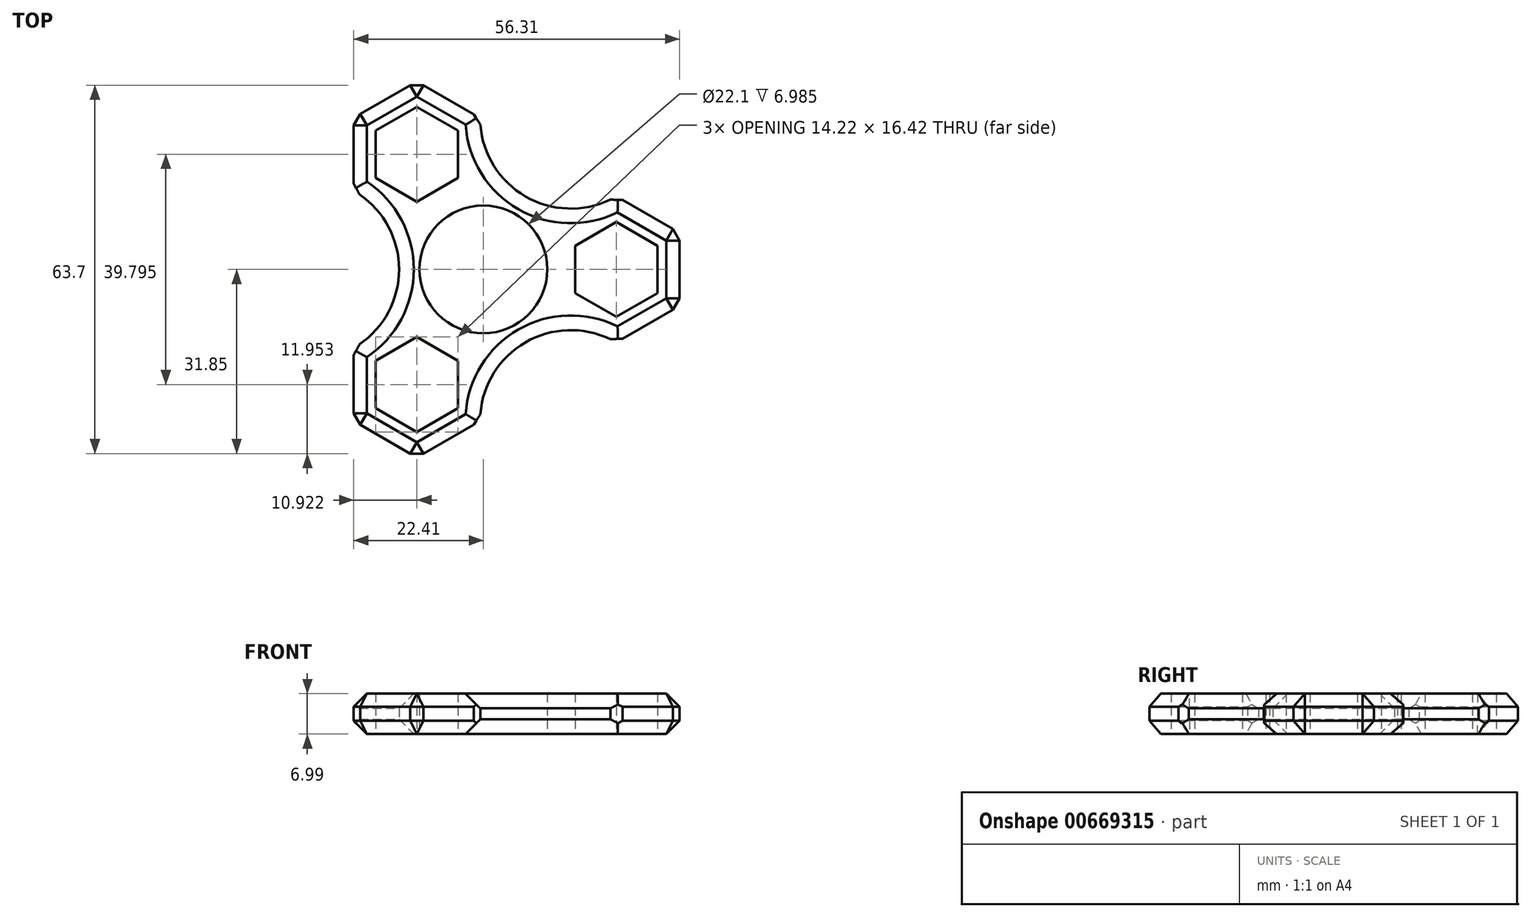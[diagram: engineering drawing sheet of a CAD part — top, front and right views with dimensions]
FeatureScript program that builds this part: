
annotation { "Feature Type Name" : "Feature", "Feature Type Description" : "" }
export const myFeature = defineFeature(function(context is Context, id is Id, definition is map)
    precondition{}
    {
        {
            var Q0;
            Q0=qCreatedBy(makeId("Top.planeOp"),FACE);
            var sketch = newSketch(context, id + "F0", { "sketchPlane" : qUnion([Q0])});
            skCircle(sketch, "E0", {"center": v(0, 0) * mm, "radius": 11.05 * mm});
            skLineSegment(sketch, "E1.0", {"start": v(15.86, -4.1) * mm, "end": v(15.86, 4.1) * mm});
            skLineSegment(sketch, "E1.1", {"start": v(15.86, 4.1) * mm, "end": v(22.98, 8.21) * mm});
            skLineSegment(sketch, "E1.2", {"start": v(22.98, 8.21) * mm, "end": v(30.09, 4.1) * mm});
            skLineSegment(sketch, "E1.3", {"start": v(30.09, 4.1) * mm, "end": v(30.09, -4.1) * mm});
            skLineSegment(sketch, "E1.4", {"start": v(30.09, -4.1) * mm, "end": v(22.98, -8.21) * mm});
            skLineSegment(sketch, "E1.5", {"start": v(22.98, -8.21) * mm, "end": v(15.86, -4.1) * mm});
            skPoint(sketch, "E1.0.midPoint", {"position": v(15.86, 0) * mm});
            skPoint(sketch, "E2.1.0", {"position": v(-7.93, 13.74) * mm});
            skLineSegment(sketch, "E2.1.1", {"start": v(-4.38, 24) * mm, "end": v(-4.38, 15.8) * mm});
            skLineSegment(sketch, "E2.1.2", {"start": v(-11.49, 28.1) * mm, "end": v(-4.38, 24) * mm});
            skLineSegment(sketch, "E2.1.3", {"start": v(-18.6, 24) * mm, "end": v(-11.49, 28.1) * mm});
            skLineSegment(sketch, "E2.1.4", {"start": v(-18.6, 15.8) * mm, "end": v(-18.6, 24) * mm});
            skLineSegment(sketch, "E2.1.5", {"start": v(-11.49, 11.69) * mm, "end": v(-18.6, 15.8) * mm});
            skLineSegment(sketch, "E2.1.6", {"start": v(-4.38, 15.8) * mm, "end": v(-11.49, 11.69) * mm});
            skPoint(sketch, "E2.2.0", {"position": v(-7.93, -13.74) * mm});
            skLineSegment(sketch, "E2.2.1", {"start": v(-18.6, -15.8) * mm, "end": v(-11.49, -11.69) * mm});
            skLineSegment(sketch, "E2.2.2", {"start": v(-18.6, -24) * mm, "end": v(-18.6, -15.8) * mm});
            skLineSegment(sketch, "E2.2.3", {"start": v(-11.49, -28.1) * mm, "end": v(-18.6, -24) * mm});
            skLineSegment(sketch, "E2.2.4", {"start": v(-4.38, -24) * mm, "end": v(-11.49, -28.1) * mm});
            skLineSegment(sketch, "E2.2.5", {"start": v(-4.38, -15.8) * mm, "end": v(-4.38, -24) * mm});
            skLineSegment(sketch, "E2.2.6", {"start": v(-11.49, -11.69) * mm, "end": v(-4.38, -15.8) * mm});
            skLineSegment(sketch, "E3.0", {"start": v(-0.57, 26.2) * mm, "end": v(-0.57, 26.2) * mm});
            skLineSegment(sketch, "E3.2", {"start": v(-22.4, 13.6) * mm, "end": v(-22.4, 26.2) * mm});
            skLineSegment(sketch, "E3.4", {"start": v(-22.4, 26.2) * mm, "end": v(-11.49, 32.5) * mm});
            skLineSegment(sketch, "E3.5", {"start": v(-11.49, 32.5) * mm, "end": v(-0.57, 26.2) * mm});
            skLineSegment(sketch, "E4.2", {"start": v(22.98, 12.61) * mm, "end": v(33.9, 6.3) * mm});
            skLineSegment(sketch, "E4.4", {"start": v(33.9, 6.3) * mm, "end": v(33.9, -6.3) * mm});
            skLineSegment(sketch, "E4.5", {"start": v(33.9, -6.3) * mm, "end": v(22.98, -12.6) * mm});
            skLineSegment(sketch, "E5.0", {"start": v(-0.57, -26.2) * mm, "end": v(-11.49, -32.5) * mm});
            skLineSegment(sketch, "E5.1", {"start": v(-22.4, -26.2) * mm, "end": v(-22.4, -13.6) * mm});
            skLineSegment(sketch, "E5.3", {"start": v(-11.49, -32.5) * mm, "end": v(-22.4, -26.2) * mm});
            skArc(sketch, "E6", {"start": v(-22.4, -13.6) * mm, "mid": v(-14.56, 0) * mm, "end": v(-22.4, 13.6) * mm});
            skArc(sketch, "E7", {"start": v(22.98, -12.6) * mm, "mid": v(7.28, -12.6) * mm, "end": v(-0.57, -26.2) * mm});
            skArc(sketch, "E8", {"start": v(-0.57, 26.2) * mm, "mid": v(7.28, 12.61) * mm, "end": v(22.98, 12.61) * mm});
            skSolve(sketch);
        }
        {
            var Q0;
            Q0=makeQuery(id+"F0.imprint","IMPRINT",FACE,{"disambiguationData":[TD([[makeQuery(id+"F0.imprint","IMPRINT",EDGE,{"derivedFrom":sQuery(id+"F0.wireOp",EDGE,"E0")}),-1.0]])]});
            extrude(context, id + "F1", {"entities" : qUnion([Q0]), "depth" : 7 * mm, "offsetDistance" : 25.4 * mm});
        }
        {
            var Q0;
            Q0=makeQuery(id+"F1.opExtrude","CAP_EDGE",EDGE,{"disambiguationData":[OSD([sQuery(id+"F0.wireOp",EDGE,"E3.5")])],"isStart":true});
            var Q1;
            Q1=makeQuery(id+"F1.opExtrude","CAP_EDGE",EDGE,{"disambiguationData":[OSD([sQuery(id+"F0.wireOp",EDGE,"E3.4")])],"isStart":true});
            var Q2;
            Q2=makeQuery(id+"F1.opExtrude","CAP_EDGE",EDGE,{"disambiguationData":[OSD([sQuery(id+"F0.wireOp",EDGE,"E3.2")])],"isStart":true});
            var Q3;
            Q3=makeQuery(id+"F1.opExtrude","CAP_EDGE",EDGE,{"disambiguationData":[OSD([sQuery(id+"F0.wireOp",EDGE,"E5.3")])],"isStart":true});
            var Q4;
            Q4=makeQuery(id+"F1.opExtrude","CAP_EDGE",EDGE,{"disambiguationData":[OSD([sQuery(id+"F0.wireOp",EDGE,"E5.1")])],"isStart":true});
            var Q5;
            Q5=makeQuery(id+"F1.opExtrude","CAP_EDGE",EDGE,{"disambiguationData":[OSD([sQuery(id+"F0.wireOp",EDGE,"E5.0")])],"isStart":true});
            var Q6;
            Q6=makeQuery(id+"F1.opExtrude","CAP_EDGE",EDGE,{"disambiguationData":[OSD([sQuery(id+"F0.wireOp",EDGE,"E4.5")])],"isStart":true});
            var Q7;
            Q7=makeQuery(id+"F1.opExtrude","CAP_EDGE",EDGE,{"disambiguationData":[OSD([sQuery(id+"F0.wireOp",EDGE,"E4.4")])],"isStart":true});
            var Q8;
            Q8=makeQuery(id+"F1.opExtrude","CAP_EDGE",EDGE,{"disambiguationData":[OSD([sQuery(id+"F0.wireOp",EDGE,"E4.2")])],"isStart":true});
            var Q9;
            Q9=makeQuery(id+"F1.opExtrude","CAP_EDGE",EDGE,{"disambiguationData":[OSD([sQuery(id+"F0.wireOp",EDGE,"E3.5")])],"isStart":false});
            var Q10;
            Q10=makeQuery(id+"F1.opExtrude","CAP_EDGE",EDGE,{"disambiguationData":[OSD([sQuery(id+"F0.wireOp",EDGE,"E3.4")])],"isStart":false});
            var Q11;
            Q11=makeQuery(id+"F1.opExtrude","CAP_EDGE",EDGE,{"disambiguationData":[OSD([sQuery(id+"F0.wireOp",EDGE,"E3.2")])],"isStart":false});
            var Q12;
            Q12=makeQuery(id+"F1.opExtrude","CAP_EDGE",EDGE,{"disambiguationData":[OSD([sQuery(id+"F0.wireOp",EDGE,"E4.2")])],"isStart":false});
            var Q13;
            Q13=makeQuery(id+"F1.opExtrude","CAP_EDGE",EDGE,{"disambiguationData":[OSD([sQuery(id+"F0.wireOp",EDGE,"E4.4")])],"isStart":false});
            var Q14;
            Q14=makeQuery(id+"F1.opExtrude","CAP_EDGE",EDGE,{"disambiguationData":[OSD([sQuery(id+"F0.wireOp",EDGE,"E4.5")])],"isStart":false});
            var Q15;
            Q15=makeQuery(id+"F1.opExtrude","SWEPT_EDGE",EDGE,{"disambiguationData":[OSD([sQuery(id+"F0.wireOp",EDGE,"E4.4"),sQuery(id+"F0.wireOp",EDGE,"E4.5")])]});
            var Q16;
            Q16=makeQuery(id+"F1.opExtrude","CAP_EDGE",EDGE,{"disambiguationData":[OSD([sQuery(id+"F0.wireOp",EDGE,"E5.0")])],"isStart":false});
            var Q17;
            Q17=makeQuery(id+"F1.opExtrude","CAP_EDGE",EDGE,{"disambiguationData":[OSD([sQuery(id+"F0.wireOp",EDGE,"E5.3")])],"isStart":false});
            var Q18;
            Q18=makeQuery(id+"F1.opExtrude","CAP_EDGE",EDGE,{"disambiguationData":[OSD([sQuery(id+"F0.wireOp",EDGE,"E5.1")])],"isStart":false});
            var Q19;
            Q19=makeQuery(id+"F1.opExtrude","SWEPT_EDGE",EDGE,{"disambiguationData":[OSD([sQuery(id+"F0.wireOp",EDGE,"E4.2"),sQuery(id+"F0.wireOp",EDGE,"E4.4")])]});
            var Q20;
            Q20=makeQuery(id+"F1.opExtrude","SWEPT_EDGE",EDGE,{"disambiguationData":[OSD([sQuery(id+"F0.wireOp",EDGE,"E4.2"),sQuery(id+"F0.wireOp",EDGE,"E8")])]});
            var Q21;
            Q21=makeQuery(id+"F1.opExtrude","SWEPT_EDGE",EDGE,{"disambiguationData":[OSD([sQuery(id+"F0.wireOp",EDGE,"E4.5"),sQuery(id+"F0.wireOp",EDGE,"E7")])]});
            var Q22;
            Q22=makeQuery(id+"F1.opExtrude","SWEPT_EDGE",EDGE,{"disambiguationData":[OSD([sQuery(id+"F0.wireOp",EDGE,"E3.4"),sQuery(id+"F0.wireOp",EDGE,"E3.5")])]});
            var Q23;
            Q23=makeQuery(id+"F1.opExtrude","SWEPT_EDGE",EDGE,{"disambiguationData":[OSD([sQuery(id+"F0.wireOp",EDGE,"E3.2"),sQuery(id+"F0.wireOp",EDGE,"E3.4")])]});
            var Q24;
            Q24=makeQuery(id+"F1.opExtrude","SWEPT_EDGE",EDGE,{"disambiguationData":[OSD([sQuery(id+"F0.wireOp",EDGE,"E3.5"),sQuery(id+"F0.wireOp",EDGE,"E8")])]});
            var Q25;
            Q25=makeQuery(id+"F1.opExtrude","SWEPT_EDGE",EDGE,{"disambiguationData":[OSD([sQuery(id+"F0.wireOp",EDGE,"E3.2"),sQuery(id+"F0.wireOp",EDGE,"E6")])]});
            var Q26;
            Q26=makeQuery(id+"F1.opExtrude","SWEPT_EDGE",EDGE,{"disambiguationData":[OSD([sQuery(id+"F0.wireOp",EDGE,"E5.1"),sQuery(id+"F0.wireOp",EDGE,"E6")])]});
            var Q27;
            Q27=makeQuery(id+"F1.opExtrude","SWEPT_EDGE",EDGE,{"disambiguationData":[OSD([sQuery(id+"F0.wireOp",EDGE,"E5.1"),sQuery(id+"F0.wireOp",EDGE,"E5.3")])]});
            var Q28;
            Q28=makeQuery(id+"F1.opExtrude","SWEPT_EDGE",EDGE,{"disambiguationData":[OSD([sQuery(id+"F0.wireOp",EDGE,"E5.0"),sQuery(id+"F0.wireOp",EDGE,"E5.3")])]});
            var Q29;
            Q29=makeQuery(id+"F1.opExtrude","SWEPT_EDGE",EDGE,{"disambiguationData":[OSD([sQuery(id+"F0.wireOp",EDGE,"E5.0"),sQuery(id+"F0.wireOp",EDGE,"E7")])]});
            chamfer(context, id + "F2", {"entities" : qUnion([Q0, Q1, Q2, Q3, Q4, Q5, Q6, Q7, Q8, Q9, Q10, Q11, Q12, Q13, Q14, Q15, Q16, Q17, Q18, Q19, Q20, Q21, Q22, Q23, Q24, Q25, Q26, Q27, Q28, Q29]), "width" : 2.3 * mm, "tangentPropagation" : true});
        }
        {
            var Q0;
            Q0=makeQuery(id+"F1.opExtrude","CAP_EDGE",EDGE,{"disambiguationData":[OSD([sQuery(id+"F0.wireOp",EDGE,"E7")])],"isStart":false});
            var Q1;
            Q1=makeQuery(id+"F1.opExtrude","CAP_EDGE",EDGE,{"disambiguationData":[OSD([sQuery(id+"F0.wireOp",EDGE,"E7")])],"isStart":true});
            var Q2;
            Q2=makeQuery(id+"F1.opExtrude","CAP_EDGE",EDGE,{"disambiguationData":[OSD([sQuery(id+"F0.wireOp",EDGE,"E6")])],"isStart":true});
            var Q3;
            Q3=makeQuery(id+"F1.opExtrude","CAP_EDGE",EDGE,{"disambiguationData":[OSD([sQuery(id+"F0.wireOp",EDGE,"E6")])],"isStart":false});
            var Q4;
            Q4=makeQuery(id+"F1.opExtrude","CAP_EDGE",EDGE,{"disambiguationData":[OSD([sQuery(id+"F0.wireOp",EDGE,"E8")])],"isStart":false});
            var Q5;
            Q5=makeQuery(id+"F1.opExtrude","CAP_EDGE",EDGE,{"disambiguationData":[OSD([sQuery(id+"F0.wireOp",EDGE,"E8")])],"isStart":true});
            chamfer(context, id + "F3", {"entities" : qUnion([Q0, Q1, Q2, Q3, Q4, Q5]), "width" : 2.54 * mm, "tangentPropagation" : true});
        }
    });
